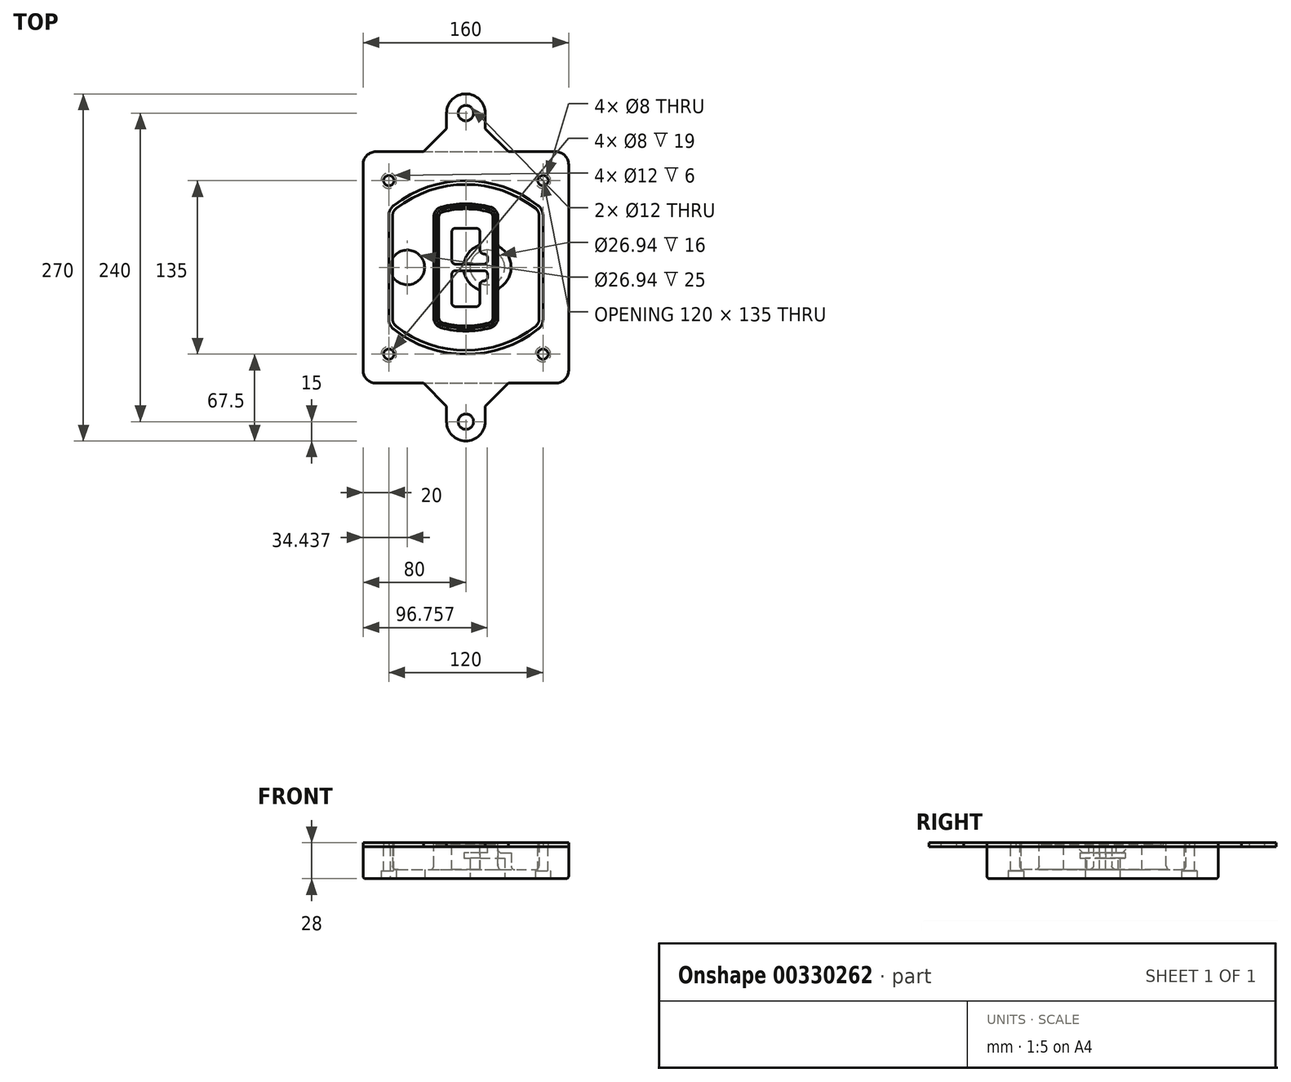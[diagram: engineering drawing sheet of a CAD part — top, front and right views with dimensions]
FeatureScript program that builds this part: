
annotation { "Feature Type Name" : "Feature", "Feature Type Description" : "" }
export const myFeature = defineFeature(function(context is Context, id is Id, definition is map)
    precondition{}
    {
        {
            var Q0;
            Q0=qCreatedBy(makeId("Top.planeOp"),FACE);
            var sketch = newSketch(context, id + "F0", { "sketchPlane" : qUnion([Q0])});
            skPoint(sketch, "E0.rect.middle", {"position": v(0, 0) * mm});
            skLineSegment(sketch, "E1.bottom", {"start": v(-70, -90) * mm, "end": v(70, -90) * mm});
            skLineSegment(sketch, "E1.top", {"start": v(-70, 90) * mm, "end": v(70, 90) * mm});
            skLineSegment(sketch, "E1.left", {"start": v(-80, -80) * mm, "end": v(-80, 80) * mm});
            skLineSegment(sketch, "E1.right", {"start": v(80, -80) * mm, "end": v(80, 80) * mm});
            skLineSegment(sketch, "E2", {"start": v(-80, 90) * mm, "end": v(80, -90) * mm, "construction": true});
            skLineSegment(sketch, "E3", {"start": v(80, 90) * mm, "end": v(-80, -90) * mm, "construction": true});
            skCircle(sketch, "E4", {"center": v(-60, 67.5) * mm, "radius": 4 * mm});
            skCircle(sketch, "E5", {"center": v(60, 67.5) * mm, "radius": 4 * mm});
            skCircle(sketch, "E6", {"center": v(60, -67.5) * mm, "radius": 4 * mm});
            skCircle(sketch, "E7", {"center": v(-60, -67.5) * mm, "radius": 4 * mm});
            skLineSegment(sketch, "E8", {"start": v(-60, 67.5) * mm, "end": v(60, 67.5) * mm, "construction": true});
            skLineSegment(sketch, "E9", {"start": v(60, 67.5) * mm, "end": v(60, -67.5) * mm, "construction": true});
            skLineSegment(sketch, "E10", {"start": v(60, -67.5) * mm, "end": v(-60, -67.5) * mm, "construction": true});
            skLineSegment(sketch, "E11", {"start": v(-60, -67.5) * mm, "end": v(-60, 67.5) * mm, "construction": true});
            skLineSegment(sketch, "E12", {"start": v(-60, 40.3) * mm, "end": v(-60, -40.3) * mm});
            skLineSegment(sketch, "E13", {"start": v(60, 40.3) * mm, "end": v(60, -40.3) * mm});
            skArc(sketch, "E14", {"start": v(56.15, 48.18) * mm, "mid": v(0, 67.5) * mm, "end": v(-56.15, 48.18) * mm});
            skArc(sketch, "E15", {"start": v(-56.15, -48.18) * mm, "mid": v(0, -67.5) * mm, "end": v(56.15, -48.18) * mm});
            skLineSegment(sketch, "E16", {"start": v(-60, 0) * mm, "end": v(60, 0) * mm, "construction": true});
            skPoint(sketch, "E17.visualSharp", {"position": v(-60, -45) * mm});
            skArc(sketch, "E17.filletArc", {"start": v(-60, -40.3) * mm, "mid": v(-58.99, -44.68) * mm, "end": v(-56.15, -48.18) * mm});
            skPoint(sketch, "E18.visualSharp", {"position": v(-60, 45) * mm});
            skArc(sketch, "E18.filletArc", {"start": v(-56.15, 48.18) * mm, "mid": v(-58.99, 44.68) * mm, "end": v(-60, 40.3) * mm});
            skPoint(sketch, "E19.visualSharp", {"position": v(60, 45) * mm});
            skArc(sketch, "E19.filletArc", {"start": v(60, 40.3) * mm, "mid": v(58.99, 44.68) * mm, "end": v(56.15, 48.18) * mm});
            skPoint(sketch, "E20.visualSharp", {"position": v(60, -45) * mm});
            skArc(sketch, "E20.filletArc", {"start": v(56.15, -48.18) * mm, "mid": v(58.99, -44.68) * mm, "end": v(60, -40.3) * mm});
            skPoint(sketch, "E21.visualSharp", {"position": v(-80, 90) * mm});
            skArc(sketch, "E21.filletArc", {"start": v(-70, 90) * mm, "mid": v(-77.07, 87.07) * mm, "end": v(-80, 80) * mm});
            skPoint(sketch, "E22.visualSharp", {"position": v(80, 90) * mm});
            skArc(sketch, "E22.filletArc", {"start": v(80, 80) * mm, "mid": v(77.07, 87.07) * mm, "end": v(70, 90) * mm});
            skPoint(sketch, "E23.visualSharp", {"position": v(80, -90) * mm});
            skArc(sketch, "E23.filletArc", {"start": v(70, -90) * mm, "mid": v(77.07, -87.07) * mm, "end": v(80, -80) * mm});
            skPoint(sketch, "E24.visualSharp", {"position": v(-80, -90) * mm});
            skArc(sketch, "E24.filletArc", {"start": v(-80, -80) * mm, "mid": v(-77.07, -87.07) * mm, "end": v(-70, -90) * mm});
            skArc(sketch, "E25.0", {"start": v(57, 40.3) * mm, "mid": v(56.3, 43.36) * mm, "end": v(54.3, 45.81) * mm});
            skLineSegment(sketch, "E25.1", {"start": v(57, 40.3) * mm, "end": v(57, -40.3) * mm});
            skArc(sketch, "E25.2", {"start": v(54.3, -45.81) * mm, "mid": v(56.3, -43.36) * mm, "end": v(57, -40.3) * mm});
            skArc(sketch, "E25.3", {"start": v(-54.3, -45.81) * mm, "mid": v(0, -64.5) * mm, "end": v(54.3, -45.81) * mm});
            skArc(sketch, "E25.4", {"start": v(-57, -40.3) * mm, "mid": v(-56.3, -43.36) * mm, "end": v(-54.3, -45.81) * mm});
            skArc(sketch, "E25.5", {"start": v(54.3, 45.81) * mm, "mid": v(0, 64.5) * mm, "end": v(-54.3, 45.81) * mm});
            skLineSegment(sketch, "E25.6", {"start": v(-57, 40.3) * mm, "end": v(-57, -40.3) * mm});
            skArc(sketch, "E25.7", {"start": v(-54.3, 45.81) * mm, "mid": v(-56.3, 43.36) * mm, "end": v(-57, 40.3) * mm});
            skArc(sketch, "E26.0", {"start": v(-58.62, 51.33) * mm, "mid": v(-62.58, 46.43) * mm, "end": v(-64, 40.3) * mm});
            skArc(sketch, "E26.1", {"start": v(58.62, 51.33) * mm, "mid": v(0, 71.5) * mm, "end": v(-58.62, 51.33) * mm});
            skArc(sketch, "E26.2", {"start": v(64, 40.3) * mm, "mid": v(62.58, 46.43) * mm, "end": v(58.62, 51.33) * mm});
            skLineSegment(sketch, "E26.3", {"start": v(64, 40.3) * mm, "end": v(64, -40.3) * mm});
            skArc(sketch, "E26.4", {"start": v(58.62, -51.33) * mm, "mid": v(62.58, -46.43) * mm, "end": v(64, -40.3) * mm});
            skLineSegment(sketch, "E26.5", {"start": v(-64, 40.3) * mm, "end": v(-64, -40.3) * mm});
            skArc(sketch, "E26.6", {"start": v(-58.62, -51.33) * mm, "mid": v(0, -71.5) * mm, "end": v(58.62, -51.33) * mm});
            skArc(sketch, "E26.7", {"start": v(-64, -40.3) * mm, "mid": v(-62.58, -46.43) * mm, "end": v(-58.62, -51.33) * mm});
            skSolve(sketch);
        }
        {
            var Q0;
            Q0=makeQuery(id+"F0.imprint","IMPRINT",FACE,{"disambiguationData":[TD([[makeQuery(id+"F0.imprint","IMPRINT",EDGE,{"derivedFrom":sQuery(id+"F0.wireOp",EDGE,"E1.bottom")}),1.0]])]});
            var Q1;
            Q1=makeQuery(id+"F0.imprint","IMPRINT",FACE,{"disambiguationData":[TD([[makeQuery(id+"F0.imprint","IMPRINT",EDGE,{"derivedFrom":sQuery(id+"F0.wireOp",EDGE,"E12")}),1.0]])]});
            var Q2;
            Q2=makeQuery(id+"F0.imprint","IMPRINT",FACE,{"disambiguationData":[TD([[makeQuery(id+"F0.imprint","IMPRINT",EDGE,{"derivedFrom":sQuery(id+"F0.wireOp",EDGE,"E25.0")}),1.0]])]});
            var Q3;
            Q3=makeQuery(id+"F0.imprint","IMPRINT",FACE,{"disambiguationData":[TD([[makeQuery(id+"F0.imprint","IMPRINT",EDGE,{"derivedFrom":sQuery(id+"F0.wireOp",EDGE,"E12")}),-1.0]])]});
            extrude(context, id + "F1", {"entities" : qUnion([Q0, Q1, Q2, Q3]), "oppositeDirection" : true, "depth" : 25 * mm});
        }
        {
            var Q0;
            Q0=makeQuery(id+"F0.imprint","IMPRINT",FACE,{"disambiguationData":[TD([[makeQuery(id+"F0.imprint","IMPRINT",EDGE,{"derivedFrom":sQuery(id+"F0.wireOp",EDGE,"E12")}),1.0]])]});
            extrude(context, id + "F2", {"entities" : qUnion([Q0]), "operationType" : NewBodyOperationType.ADD, "depth" : 3 * mm});
        }
        {
            var Q0;
            Q0=makeQuery(id+"F0.imprint","IMPRINT",FACE,{"disambiguationData":[TD([[makeQuery(id+"F0.imprint","IMPRINT",EDGE,{"derivedFrom":sQuery(id+"F0.wireOp",EDGE,"E25.0")}),1.0]])]});
            extrude(context, id + "F3", {"entities" : qUnion([Q0]), "operationType" : NewBodyOperationType.REMOVE, "oppositeDirection" : true, "depth" : 18 * mm});
        }
        {
            var Q0;
            Q0=makeQuery(id+"F2.opExtrude","CAP_FACE",FACE,{"disambiguationData":[OSD([sQuery(id+"F0.wireOp",EDGE,"E12"),sQuery(id+"F0.wireOp",EDGE,"E13"),sQuery(id+"F0.wireOp",EDGE,"E14"),sQuery(id+"F0.wireOp",EDGE,"E15"),sQuery(id+"F0.wireOp",EDGE,"E17.filletArc"),sQuery(id+"F0.wireOp",EDGE,"E18.filletArc"),sQuery(id+"F0.wireOp",EDGE,"E19.filletArc"),sQuery(id+"F0.wireOp",EDGE,"E20.filletArc"),sQuery(id+"F0.wireOp",EDGE,"E25.0"),sQuery(id+"F0.wireOp",EDGE,"E25.1"),sQuery(id+"F0.wireOp",EDGE,"E25.2"),sQuery(id+"F0.wireOp",EDGE,"E25.3"),sQuery(id+"F0.wireOp",EDGE,"E25.4"),sQuery(id+"F0.wireOp",EDGE,"E25.5"),sQuery(id+"F0.wireOp",EDGE,"E25.6"),sQuery(id+"F0.wireOp",EDGE,"E25.7")])],"isStart":false});
            var sketch = newSketch(context, id + "F4", { "sketchPlane" : qUnion([Q0])});
            skArc(sketch, "E27.0", {"start": v(-19.08, -46.97) * mm, "mid": v(0, -49.5) * mm, "end": v(19.08, -46.97) * mm});
            skArc(sketch, "E28.0", {"start": v(19.08, 46.97) * mm, "mid": v(0, 49.5) * mm, "end": v(-19.08, 46.97) * mm});
            skLineSegment(sketch, "E29", {"start": v(-25, 39.25) * mm, "end": v(-25, -39.25) * mm});
            skLineSegment(sketch, "E30", {"start": v(25, 39.25) * mm, "end": v(25, -39.25) * mm});
            skLineSegment(sketch, "E31", {"start": v(-25, 45.1) * mm, "end": v(25, 45.1) * mm, "construction": true});
            skLineSegment(sketch, "E32", {"start": v(-25, -45.1) * mm, "end": v(25, -45.1) * mm, "construction": true});
            skPoint(sketch, "E33.visualSharp", {"position": v(-25, 45.1) * mm});
            skArc(sketch, "E33.filletArc", {"start": v(-19.08, 46.97) * mm, "mid": v(-23.35, 44.11) * mm, "end": v(-25, 39.25) * mm});
            skPoint(sketch, "E34.visualSharp", {"position": v(25, 45.1) * mm});
            skArc(sketch, "E34.filletArc", {"start": v(25, 39.25) * mm, "mid": v(23.35, 44.11) * mm, "end": v(19.08, 46.97) * mm});
            skPoint(sketch, "E35.visualSharp", {"position": v(25, -45.1) * mm});
            skArc(sketch, "E35.filletArc", {"start": v(19.08, -46.97) * mm, "mid": v(23.35, -44.11) * mm, "end": v(25, -39.25) * mm});
            skPoint(sketch, "E36.visualSharp", {"position": v(-25, -45.1) * mm});
            skArc(sketch, "E36.filletArc", {"start": v(-25, -39.25) * mm, "mid": v(-23.35, -44.11) * mm, "end": v(-19.08, -46.97) * mm});
            skArc(sketch, "E37.0", {"start": v(54.3, 45.81) * mm, "mid": v(0, 64.5) * mm, "end": v(-54.3, 45.81) * mm});
            skArc(sketch, "E37.1", {"start": v(-54.3, 45.81) * mm, "mid": v(-56.3, 43.36) * mm, "end": v(-57, 40.3) * mm});
            skLineSegment(sketch, "E37.2", {"start": v(-57, 40.3) * mm, "end": v(-57, -40.3) * mm});
            skArc(sketch, "E37.3", {"start": v(-57, -40.3) * mm, "mid": v(-56.3, -43.36) * mm, "end": v(-54.3, -45.81) * mm});
            skArc(sketch, "E37.4", {"start": v(-54.3, -45.81) * mm, "mid": v(0, -64.5) * mm, "end": v(54.3, -45.81) * mm});
            skArc(sketch, "E37.5", {"start": v(54.3, -45.81) * mm, "mid": v(56.3, -43.36) * mm, "end": v(57, -40.3) * mm});
            skLineSegment(sketch, "E37.6", {"start": v(57, 40.3) * mm, "end": v(57, -40.3) * mm});
            skArc(sketch, "E37.7", {"start": v(57, 40.3) * mm, "mid": v(56.3, 43.36) * mm, "end": v(54.3, 45.81) * mm});
            skLineSegment(sketch, "E38.0", {"start": v(23, 39.25) * mm, "end": v(23, -39.25) * mm});
            skArc(sketch, "E38.1", {"start": v(18.56, -45.04) * mm, "mid": v(21.76, -42.9) * mm, "end": v(23, -39.25) * mm});
            skArc(sketch, "E38.2", {"start": v(-18.56, -45.04) * mm, "mid": v(0, -47.5) * mm, "end": v(18.56, -45.04) * mm});
            skArc(sketch, "E38.3", {"start": v(-23, -39.25) * mm, "mid": v(-21.76, -42.9) * mm, "end": v(-18.56, -45.04) * mm});
            skLineSegment(sketch, "E38.4", {"start": v(-23, 39.25) * mm, "end": v(-23, -39.25) * mm});
            skArc(sketch, "E38.5", {"start": v(23, 39.25) * mm, "mid": v(21.76, 42.9) * mm, "end": v(18.56, 45.04) * mm});
            skArc(sketch, "E38.6", {"start": v(-18.56, 45.04) * mm, "mid": v(-21.76, 42.9) * mm, "end": v(-23, 39.25) * mm});
            skArc(sketch, "E38.7", {"start": v(18.56, 45.04) * mm, "mid": v(0, 47.5) * mm, "end": v(-18.56, 45.04) * mm});
            skArc(sketch, "E39.0", {"start": v(21, 39.25) * mm, "mid": v(20.18, 41.68) * mm, "end": v(18.04, 43.1) * mm});
            skLineSegment(sketch, "E39.1", {"start": v(21, 39.25) * mm, "end": v(21, -39.25) * mm});
            skArc(sketch, "E39.2", {"start": v(18.04, -43.1) * mm, "mid": v(20.18, -41.68) * mm, "end": v(21, -39.25) * mm});
            skArc(sketch, "E39.3", {"start": v(-18.04, -43.1) * mm, "mid": v(0, -45.5) * mm, "end": v(18.04, -43.1) * mm});
            skArc(sketch, "E39.4", {"start": v(-21, -39.25) * mm, "mid": v(-20.18, -41.68) * mm, "end": v(-18.04, -43.1) * mm});
            skArc(sketch, "E39.5", {"start": v(18.04, 43.1) * mm, "mid": v(0, 45.5) * mm, "end": v(-18.04, 43.1) * mm});
            skLineSegment(sketch, "E39.6", {"start": v(-21, 39.25) * mm, "end": v(-21, -39.25) * mm});
            skArc(sketch, "E39.7", {"start": v(-18.04, 43.1) * mm, "mid": v(-20.18, 41.68) * mm, "end": v(-21, 39.25) * mm});
            skLineSegment(sketch, "E40", {"start": v(-25, 0) * mm, "end": v(25, 0) * mm, "construction": true});
            skLineSegment(sketch, "E41", {"start": v(-11, 5.5) * mm, "end": v(-11, 27.5) * mm});
            skLineSegment(sketch, "E42", {"start": v(-8, 30.5) * mm, "end": v(8, 30.5) * mm});
            skLineSegment(sketch, "E43", {"start": v(11, 27.5) * mm, "end": v(11, 13.5) * mm});
            skLineSegment(sketch, "E44", {"start": v(14, 10.5) * mm, "end": v(14, 10.5) * mm});
            skLineSegment(sketch, "E45", {"start": v(17, 7.5) * mm, "end": v(17, 5.5) * mm});
            skLineSegment(sketch, "E46", {"start": v(14, 2.5) * mm, "end": v(-8, 2.5) * mm});
            skPoint(sketch, "E47.visualSharp", {"position": v(-11, 30.5) * mm});
            skArc(sketch, "E47.filletArc", {"start": v(-8, 30.5) * mm, "mid": v(-10.12, 29.62) * mm, "end": v(-11, 27.5) * mm});
            skPoint(sketch, "E48.visualSharp", {"position": v(11, 30.5) * mm});
            skArc(sketch, "E48.filletArc", {"start": v(11, 27.5) * mm, "mid": v(10.12, 29.62) * mm, "end": v(8, 30.5) * mm});
            skPoint(sketch, "E49.visualSharp", {"position": v(11, 10.5) * mm});
            skArc(sketch, "E49.filletArc", {"start": v(11, 13.5) * mm, "mid": v(11.88, 11.38) * mm, "end": v(14, 10.5) * mm});
            skPoint(sketch, "E50.visualSharp", {"position": v(17, 10.5) * mm});
            skArc(sketch, "E50.filletArc", {"start": v(17, 7.5) * mm, "mid": v(16.12, 9.62) * mm, "end": v(14, 10.5) * mm});
            skPoint(sketch, "E51.visualSharp", {"position": v(17, 2.5) * mm});
            skArc(sketch, "E51.filletArc", {"start": v(14, 2.5) * mm, "mid": v(16.12, 3.38) * mm, "end": v(17, 5.5) * mm});
            skPoint(sketch, "E52.visualSharp", {"position": v(-11, 2.5) * mm});
            skArc(sketch, "E52.filletArc", {"start": v(-11, 5.5) * mm, "mid": v(-10.12, 3.38) * mm, "end": v(-8, 2.5) * mm});
            skLineSegment(sketch, "E53.0.MirrorCS", {"start": v(14, -2.5) * mm, "end": v(-8, -2.5) * mm});
            skArc(sketch, "E54.0.MirrorCS", {"start": v(-11, -5.5) * mm, "mid": v(-10.12, -3.38) * mm, "end": v(-8, -2.5) * mm});
            skLineSegment(sketch, "E55.0.MirrorCS", {"start": v(-11, -5.5) * mm, "end": v(-11, -27.5) * mm});
            skArc(sketch, "E56.0.MirrorCS", {"start": v(-8, -30.5) * mm, "mid": v(-10.12, -29.62) * mm, "end": v(-11, -27.5) * mm});
            skLineSegment(sketch, "E57.0.MirrorCS", {"start": v(-8, -30.5) * mm, "end": v(8, -30.5) * mm});
            skArc(sketch, "E58.0.MirrorCS", {"start": v(11, -27.5) * mm, "mid": v(10.12, -29.62) * mm, "end": v(8, -30.5) * mm});
            skLineSegment(sketch, "E59.0.MirrorCS", {"start": v(11, -27.5) * mm, "end": v(11, -13.5) * mm});
            skArc(sketch, "E60.0.MirrorCS", {"start": v(11, -13.5) * mm, "mid": v(11.88, -11.38) * mm, "end": v(14, -10.5) * mm});
            skArc(sketch, "E61.0.MirrorCS", {"start": v(17, -7.5) * mm, "mid": v(16.12, -9.62) * mm, "end": v(14, -10.5) * mm});
            skLineSegment(sketch, "E62.0.MirrorCS", {"start": v(17, -7.5) * mm, "end": v(17, -5.5) * mm});
            skArc(sketch, "E63.0.MirrorCS", {"start": v(14, -2.5) * mm, "mid": v(16.12, -3.38) * mm, "end": v(17, -5.5) * mm});
            skSolve(sketch);
        }
        {
            var Q0;
            Q0=makeQuery(id+"F4.imprint","IMPRINT",FACE,{"disambiguationData":[TD([[makeQuery(id+"F4.imprint","IMPRINT",EDGE,{"derivedFrom":sQuery(id+"F4.wireOp",EDGE,"E27.0")}),1.0]])]});
            var Q1;
            Q1=makeQuery(id+"F4.imprint","IMPRINT",FACE,{"disambiguationData":[TD([[makeQuery(id+"F4.imprint","IMPRINT",EDGE,{"derivedFrom":sQuery(id+"F4.wireOp",EDGE,"E38.0")}),-1.0]])]});
            var Q2;
            Q2=makeQuery(id+"F4.imprint","IMPRINT",FACE,{"disambiguationData":[TD([[makeQuery(id+"F4.imprint","IMPRINT",EDGE,{"derivedFrom":sQuery(id+"F4.wireOp",EDGE,"E39.0")}),1.0]])]});
            extrude(context, id + "F5", {"entities" : qUnion([Q0, Q1, Q2]), "operationType" : NewBodyOperationType.ADD, "endBound" : BoundingType.UP_TO_NEXT, "oppositeDirection" : true, "depth" : 25 * mm});
        }
        {
            var Q0;
            Q0=makeQuery(id+"F4.imprint","IMPRINT",FACE,{"disambiguationData":[TD([[makeQuery(id+"F4.imprint","IMPRINT",EDGE,{"derivedFrom":sQuery(id+"F4.wireOp",EDGE,"E38.0")}),-1.0]])]});
            extrude(context, id + "F6", {"entities" : qUnion([Q0]), "operationType" : NewBodyOperationType.REMOVE, "oppositeDirection" : true, "depth" : 2 * mm});
        }
        {
            var Q0;
            Q0=makeQuery(id+"F1.opExtrude","CAP_FACE",FACE,{"disambiguationData":[OSD([sQuery(id+"F0.wireOp",EDGE,"E1.bottom"),sQuery(id+"F0.wireOp",EDGE,"E1.top"),sQuery(id+"F0.wireOp",EDGE,"E1.left"),sQuery(id+"F0.wireOp",EDGE,"E1.right"),sQuery(id+"F0.wireOp",EDGE,"E4"),sQuery(id+"F0.wireOp",EDGE,"E5"),sQuery(id+"F0.wireOp",EDGE,"E6"),sQuery(id+"F0.wireOp",EDGE,"E7"),sQuery(id+"F0.wireOp",EDGE,"E21.filletArc"),sQuery(id+"F0.wireOp",EDGE,"E22.filletArc"),sQuery(id+"F0.wireOp",EDGE,"E23.filletArc"),sQuery(id+"F0.wireOp",EDGE,"E24.filletArc")])],"isStart":false});
            var sketch = newSketch(context, id + "F7", { "sketchPlane" : qUnion([Q0])});
            skCircle(sketch, "E64", {"center": v(16.76, 0) * mm, "radius": 13.47 * mm});
            skCircle(sketch, "E65", {"center": v(-45.56, 0) * mm, "radius": 13.47 * mm});
            skLineSegment(sketch, "E66", {"start": v(80, 0) * mm, "end": v(-80, 0) * mm});
            skCircle(sketch, "E67", {"center": v(16.76, 0) * mm, "radius": 18.47 * mm});
            skCircle(sketch, "E68", {"center": v(60, -67.5) * mm, "radius": 6 * mm});
            skCircle(sketch, "E69", {"center": v(-60, -67.5) * mm, "radius": 6 * mm});
            skCircle(sketch, "E70", {"center": v(-60, 67.5) * mm, "radius": 6 * mm});
            skCircle(sketch, "E71", {"center": v(60, 67.5) * mm, "radius": 6 * mm});
            skSolve(sketch);
        }
        {
            var Q0;
            {var subQ1=sQuery(id+"F7.wireOp",EDGE,"E66");var subQ4=sQuery(id+"F7.wireOp",EDGE,"E64");var subQ6=makeQuery(id+"F7.imprint","INTERSECT",VERTEX,{"disambiguationData":[OD(0.0)],"derivedFrom":[subQ4,subQ1]});Q0=makeQuery(id+"F7.imprint","IMPRINT",FACE,{"disambiguationData":[TD([[makeQuery(id+"F7.imprint","IMPRINT",EDGE,{"disambiguationData":[TD([[subQ6,-1.0]])],"derivedFrom":subQ4}),-1.0]])]});}
            var Q1;
            {var subQ0=sQuery(id+"F7.wireOp",EDGE,"E66");var subQ1=sQuery(id+"F7.wireOp",EDGE,"E64");var subQ3=makeQuery(id+"F7.imprint","INTERSECT",VERTEX,{"disambiguationData":[OD(0.0)],"derivedFrom":[subQ1,subQ0]});Q1=makeQuery(id+"F7.imprint","IMPRINT",FACE,{"disambiguationData":[TD([[makeQuery(id+"F7.imprint","IMPRINT",EDGE,{"disambiguationData":[TD([[subQ3,-1.0]])],"derivedFrom":subQ1}),1.0]])]});}
            var Q2;
            {var subQ0=sQuery(id+"F7.wireOp",EDGE,"E66");var subQ1=sQuery(id+"F7.wireOp",EDGE,"E64");var subQ3=makeQuery(id+"F7.imprint","INTERSECT",VERTEX,{"disambiguationData":[OD(0.0)],"derivedFrom":[subQ1,subQ0]});Q2=makeQuery(id+"F7.imprint","IMPRINT",FACE,{"disambiguationData":[TD([[makeQuery(id+"F7.imprint","IMPRINT",EDGE,{"disambiguationData":[TD([[subQ3,1.0]])],"derivedFrom":subQ1}),1.0]])]});}
            var Q3;
            {var subQ1=sQuery(id+"F7.wireOp",EDGE,"E66");var subQ4=sQuery(id+"F7.wireOp",EDGE,"E64");var subQ6=makeQuery(id+"F7.imprint","INTERSECT",VERTEX,{"disambiguationData":[OD(0.0)],"derivedFrom":[subQ4,subQ1]});Q3=makeQuery(id+"F7.imprint","IMPRINT",FACE,{"disambiguationData":[TD([[makeQuery(id+"F7.imprint","IMPRINT",EDGE,{"disambiguationData":[TD([[subQ6,1.0]])],"derivedFrom":subQ4}),-1.0]])]});}
            extrude(context, id + "F8", {"entities" : qUnion([Q0, Q1, Q2, Q3]), "operationType" : NewBodyOperationType.ADD, "oppositeDirection" : true, "depth" : 20 * mm});
        }
        {
            var Q0;
            {var subQ0=sQuery(id+"F7.wireOp",EDGE,"E66");var subQ1=sQuery(id+"F7.wireOp",EDGE,"E64");var subQ3=makeQuery(id+"F7.imprint","INTERSECT",VERTEX,{"disambiguationData":[OD(0.0)],"derivedFrom":[subQ1,subQ0]});Q0=makeQuery(id+"F7.imprint","IMPRINT",FACE,{"disambiguationData":[TD([[makeQuery(id+"F7.imprint","IMPRINT",EDGE,{"disambiguationData":[TD([[subQ3,-1.0]])],"derivedFrom":subQ1}),1.0]])]});}
            var Q1;
            {var subQ0=sQuery(id+"F7.wireOp",EDGE,"E66");var subQ1=sQuery(id+"F7.wireOp",EDGE,"E64");var subQ3=makeQuery(id+"F7.imprint","INTERSECT",VERTEX,{"disambiguationData":[OD(0.0)],"derivedFrom":[subQ1,subQ0]});Q1=makeQuery(id+"F7.imprint","IMPRINT",FACE,{"disambiguationData":[TD([[makeQuery(id+"F7.imprint","IMPRINT",EDGE,{"disambiguationData":[TD([[subQ3,1.0]])],"derivedFrom":subQ1}),1.0]])]});}
            extrude(context, id + "F9", {"entities" : qUnion([Q0, Q1]), "operationType" : NewBodyOperationType.REMOVE, "oppositeDirection" : true, "depth" : 16 * mm});
        }
        {
            var Q0;
            {var subQ0=sQuery(id+"F7.wireOp",EDGE,"E66");var subQ1=sQuery(id+"F7.wireOp",EDGE,"E65");var subQ3=makeQuery(id+"F7.imprint","INTERSECT",VERTEX,{"disambiguationData":[OD(0.0)],"derivedFrom":[subQ1,subQ0]});Q0=makeQuery(id+"F7.imprint","IMPRINT",FACE,{"disambiguationData":[TD([[makeQuery(id+"F7.imprint","IMPRINT",EDGE,{"disambiguationData":[TD([[subQ3,-1.0]])],"derivedFrom":subQ1}),1.0]])]});}
            var Q1;
            {var subQ0=sQuery(id+"F7.wireOp",EDGE,"E66");var subQ1=sQuery(id+"F7.wireOp",EDGE,"E65");var subQ3=makeQuery(id+"F7.imprint","INTERSECT",VERTEX,{"disambiguationData":[OD(0.0)],"derivedFrom":[subQ1,subQ0]});Q1=makeQuery(id+"F7.imprint","IMPRINT",FACE,{"disambiguationData":[TD([[makeQuery(id+"F7.imprint","IMPRINT",EDGE,{"disambiguationData":[TD([[subQ3,1.0]])],"derivedFrom":subQ1}),1.0]])]});}
            extrude(context, id + "F10", {"entities" : qUnion([Q0, Q1]), "operationType" : NewBodyOperationType.REMOVE, "oppositeDirection" : true, "depth" : 25 * mm});
        }
        {
            var Q0;
            Q0=makeQuery(id+"F7.imprint","IMPRINT",FACE,{"disambiguationData":[TD([[makeQuery(id+"F7.imprint","IMPRINT",EDGE,{"derivedFrom":sQuery(id+"F7.wireOp",EDGE,"E68")}),1.0]])]});
            var Q1;
            Q1=makeQuery(id+"F7.imprint","IMPRINT",FACE,{"disambiguationData":[TD([[makeQuery(id+"F7.imprint","IMPRINT",EDGE,{"derivedFrom":makeQuery(id+"F1.opExtrude","CAP_EDGE",EDGE,{"disambiguationData":[OSD([sQuery(id+"F0.wireOp",EDGE,"E5")])],"isStart":false})}),-1.0]])]});
            var Q2;
            Q2=makeQuery(id+"F7.imprint","IMPRINT",FACE,{"disambiguationData":[TD([[makeQuery(id+"F7.imprint","IMPRINT",EDGE,{"derivedFrom":sQuery(id+"F7.wireOp",EDGE,"E69")}),1.0]])]});
            var Q3;
            Q3=makeQuery(id+"F7.imprint","IMPRINT",FACE,{"disambiguationData":[TD([[makeQuery(id+"F7.imprint","IMPRINT",EDGE,{"derivedFrom":makeQuery(id+"F1.opExtrude","CAP_EDGE",EDGE,{"disambiguationData":[OSD([sQuery(id+"F0.wireOp",EDGE,"E4")])],"isStart":false})}),-1.0]])]});
            var Q4;
            Q4=makeQuery(id+"F7.imprint","IMPRINT",FACE,{"disambiguationData":[TD([[makeQuery(id+"F7.imprint","IMPRINT",EDGE,{"derivedFrom":sQuery(id+"F7.wireOp",EDGE,"E70")}),1.0]])]});
            var Q5;
            Q5=makeQuery(id+"F7.imprint","IMPRINT",FACE,{"disambiguationData":[TD([[makeQuery(id+"F7.imprint","IMPRINT",EDGE,{"derivedFrom":makeQuery(id+"F1.opExtrude","CAP_EDGE",EDGE,{"disambiguationData":[OSD([sQuery(id+"F0.wireOp",EDGE,"E7")])],"isStart":false})}),-1.0]])]});
            var Q6;
            Q6=makeQuery(id+"F7.imprint","IMPRINT",FACE,{"disambiguationData":[TD([[makeQuery(id+"F7.imprint","IMPRINT",EDGE,{"derivedFrom":sQuery(id+"F7.wireOp",EDGE,"E71")}),1.0]])]});
            var Q7;
            Q7=makeQuery(id+"F7.imprint","IMPRINT",FACE,{"disambiguationData":[TD([[makeQuery(id+"F7.imprint","IMPRINT",EDGE,{"derivedFrom":makeQuery(id+"F1.opExtrude","CAP_EDGE",EDGE,{"disambiguationData":[OSD([sQuery(id+"F0.wireOp",EDGE,"E6")])],"isStart":false})}),-1.0]])]});
            extrude(context, id + "F11", {"entities" : qUnion([Q0, Q1, Q2, Q3, Q4, Q5, Q6, Q7]), "operationType" : NewBodyOperationType.REMOVE, "oppositeDirection" : true, "depth" : 6 * mm});
        }
        {
            var Q0;
            Q0=makeQuery(id+"F9.boolean.opBoolean","COPY",FACE,{"derivedFrom":makeQuery(id+"F9.opExtrude","CAP_FACE",FACE,{"disambiguationData":[OSD([sQuery(id+"F7.wireOp",EDGE,"E64")])],"isStart":false})});
            var sketch = newSketch(context, id + "F12", { "sketchPlane" : qUnion([Q0])});
            skArc(sketch, "E72.0", {"start": v(11, 17.55) * mm, "mid": v(2.57, 11.82) * mm, "end": v(-1.54, 2.5) * mm});
            skArc(sketch, "E72.1", {"start": v(-1.54, -2.5) * mm, "mid": v(2.57, -11.82) * mm, "end": v(11, -17.55) * mm});
            skLineSegment(sketch, "E73", {"start": v(-1.54, -2.5) * mm, "end": v(14, -2.5) * mm});
            skLineSegment(sketch, "E74.0", {"start": v(14, 2.5) * mm, "end": v(-1.54, 2.5) * mm});
            skArc(sketch, "E74.1", {"start": v(14, 2.5) * mm, "mid": v(16.12, 3.38) * mm, "end": v(17, 5.5) * mm});
            skLineSegment(sketch, "E74.2", {"start": v(17, 7.5) * mm, "end": v(17, 5.5) * mm});
            skArc(sketch, "E74.3", {"start": v(17, 7.5) * mm, "mid": v(16.12, 9.62) * mm, "end": v(14, 10.5) * mm});
            skArc(sketch, "E74.4", {"start": v(11, 13.5) * mm, "mid": v(11.88, 11.38) * mm, "end": v(14, 10.5) * mm});
            skLineSegment(sketch, "E74.5", {"start": v(11, 17.55) * mm, "end": v(11, 13.5) * mm});
            skLineSegment(sketch, "E74.7", {"start": v(14, -2.5) * mm, "end": v(-1.54, -2.5) * mm});
            skArc(sketch, "E74.8", {"start": v(14, -2.5) * mm, "mid": v(16.12, -3.38) * mm, "end": v(17, -5.5) * mm});
            skLineSegment(sketch, "E74.9", {"start": v(17, -7.5) * mm, "end": v(17, -5.5) * mm});
            skArc(sketch, "E74.10", {"start": v(17, -7.5) * mm, "mid": v(16.12, -9.62) * mm, "end": v(14, -10.5) * mm});
            skArc(sketch, "E74.11", {"start": v(11, -13.5) * mm, "mid": v(11.88, -11.38) * mm, "end": v(14, -10.5) * mm});
            skLineSegment(sketch, "E74.12", {"start": v(11, -17.55) * mm, "end": v(11, -13.5) * mm});
            skPoint(sketch, "E75.orphan", {"position": v(11, -27.5) * mm});
            skPoint(sketch, "E76.orphan", {"position": v(-8, -2.5) * mm});
            skPoint(sketch, "E77.orphan", {"position": v(-8, 2.5) * mm});
            skPoint(sketch, "E78.orphan", {"position": v(11, 27.5) * mm});
            skSolve(sketch);
        }
        {
            var Q0;
            {var subQ7=sQuery(id+"F12.wireOp",EDGE,"E72.0");var subQ14=sQuery(id+"F12.wireOp",EDGE,"E72.1");var subQ16=sQuery(id+"F12.wireOp",EDGE,"E74.1");var subQ18=sQuery(id+"F12.wireOp",EDGE,"E74.8");Q0=qUnion([makeQuery(id+"F12.imprint","IMPRINT",FACE,{"disambiguationData":[TD([[makeQuery(id+"F12.imprint","IMPRINT",EDGE,{"derivedFrom":subQ7}),1.0]])]}),makeQuery(id+"F12.imprint","IMPRINT",FACE,{"disambiguationData":[TD([[makeQuery(id+"F12.imprint","IMPRINT",EDGE,{"derivedFrom":subQ14}),1.0]])]}),makeQuery(id+"F12.imprint","IMPRINT",FACE,{"disambiguationData":[TD([[makeQuery(id+"F12.imprint","IMPRINT",EDGE,{"derivedFrom":subQ16}),1.0]])]}),makeQuery(id+"F12.imprint","IMPRINT",FACE,{"disambiguationData":[TD([[makeQuery(id+"F12.imprint","IMPRINT",EDGE,{"derivedFrom":subQ18}),-1.0]])]})]);}
            var Q1;
            Q1=makeQuery(id+"F5.boolean.opBoolean","SPLIT",FACE,{"disambiguationData":[TD([makeQuery(id+"F5.opExtrude","SWEPT_FACE",FACE,{"disambiguationData":[OSD([sQuery(id+"F4.wireOp",EDGE,"E41")])]})])],"derivedFrom":makeQuery(id+"F3.boolean.opBoolean","COPY",FACE,{"derivedFrom":makeQuery(id+"F3.opExtrude","CAP_FACE",FACE,{"disambiguationData":[OSD([sQuery(id+"F0.wireOp",EDGE,"E25.0"),sQuery(id+"F0.wireOp",EDGE,"E25.1"),sQuery(id+"F0.wireOp",EDGE,"E25.2"),sQuery(id+"F0.wireOp",EDGE,"E25.3"),sQuery(id+"F0.wireOp",EDGE,"E25.4"),sQuery(id+"F0.wireOp",EDGE,"E25.5"),sQuery(id+"F0.wireOp",EDGE,"E25.6"),sQuery(id+"F0.wireOp",EDGE,"E25.7")])],"isStart":false})})});
            extrude(context, id + "F13", {"entities" : qUnion([Q0]), "operationType" : NewBodyOperationType.REMOVE, "endBound" : BoundingType.UP_TO_SURFACE, "endBoundEntityFace" : qUnion([Q1]), "depth" : 25 * mm});
        }
        {
            var Q0;
            Q0=makeQuery(id+"F3.boolean.opBoolean","COPY",EDGE,{"derivedFrom":makeQuery(id+"F3.opExtrude","CAP_EDGE",EDGE,{"disambiguationData":[OSD([sQuery(id+"F0.wireOp",EDGE,"E25.6")])],"isStart":false})});
            var Q1;
            Q1=makeQuery(id+"F8.boolean.opBoolean","INTERSECT",EDGE,{"derivedFrom":[makeQuery(id+"F5.opExtrude","SWEPT_FACE",FACE,{"disambiguationData":[OSD([sQuery(id+"F4.wireOp",EDGE,"E30")])]}),makeQuery(id+"F8.opExtrude","CAP_FACE",FACE,{"disambiguationData":[OSD([sQuery(id+"F7.wireOp",EDGE,"E67")])],"isStart":false})]});
            var Q2;
            Q2=makeQuery(id+"F8.boolean.opBoolean","INTERSECT",EDGE,{"disambiguationData":[OD(1.0)],"derivedFrom":[makeQuery(id+"F5.opExtrude","SWEPT_FACE",FACE,{"disambiguationData":[OSD([sQuery(id+"F4.wireOp",EDGE,"E30")])]}),makeQuery(id+"F8.opExtrude","SWEPT_FACE",FACE,{"disambiguationData":[OSD([sQuery(id+"F7.wireOp",EDGE,"E67")])]})]});
            var Q3;
            {var subQ0=sQuery(id+"F4.wireOp",EDGE,"E30");Q3=makeQuery(id+"F8.boolean.opBoolean","SPLIT",EDGE,{"disambiguationData":[TD([makeQuery(id+"F5.opExtrude","SWEPT_FACE",FACE,{"disambiguationData":[OSD([sQuery(id+"F4.wireOp",EDGE,"E35.filletArc")])]})])],"derivedFrom":makeQuery(id+"F5.opExtrude","CAP_EDGE",EDGE,{"disambiguationData":[OSD([subQ0])],"isStart":false})});}
            var Q4;
            {var subQ0=sQuery(id+"F0.wireOp",EDGE,"E25.7");var subQ1=sQuery(id+"F0.wireOp",EDGE,"E25.1");var subQ2=sQuery(id+"F0.wireOp",EDGE,"E25.6");var subQ3=sQuery(id+"F0.wireOp",EDGE,"E25.5");var subQ4=sQuery(id+"F0.wireOp",EDGE,"E25.4");var subQ5=sQuery(id+"F0.wireOp",EDGE,"E25.0");var subQ6=sQuery(id+"F0.wireOp",EDGE,"E25.2");var subQ7=sQuery(id+"F0.wireOp",EDGE,"E25.3");Q4=makeQuery(id+"F8.boolean.opBoolean","INTERSECT",EDGE,{"derivedFrom":[makeQuery(id+"F5.boolean.opBoolean","SPLIT",FACE,{"disambiguationData":[TD([makeQuery(id+"F2.opExtrude","SWEPT_FACE",FACE,{"disambiguationData":[OSD([subQ5])]})])],"derivedFrom":makeQuery(id+"F3.boolean.opBoolean","COPY",FACE,{"derivedFrom":makeQuery(id+"F3.opExtrude","CAP_FACE",FACE,{"disambiguationData":[OSD([subQ5,subQ1,subQ6,subQ7,subQ4,subQ3,subQ2,subQ0])],"isStart":false})})}),makeQuery(id+"F8.opExtrude","SWEPT_FACE",FACE,{"disambiguationData":[OSD([sQuery(id+"F7.wireOp",EDGE,"E67")])]})]});}
            var Q5;
            Q5=makeQuery(id+"F8.boolean.opBoolean","INTERSECT",EDGE,{"disambiguationData":[OD(0.0)],"derivedFrom":[makeQuery(id+"F5.opExtrude","SWEPT_FACE",FACE,{"disambiguationData":[OSD([sQuery(id+"F4.wireOp",EDGE,"E30")])]}),makeQuery(id+"F8.opExtrude","SWEPT_FACE",FACE,{"disambiguationData":[OSD([sQuery(id+"F7.wireOp",EDGE,"E67")])]})]});
            fillet(context, id + "F14", {"entities" : qUnion([Q0, Q1, Q2, Q3, Q4, Q5]), "radius" : 3 * mm, "tangentPropagation" : true, "allowEdgeOverflow" : false});
        }
        {
            var Q0;
            Q0=makeQuery(id+"F1.opExtrude","CAP_EDGE",EDGE,{"disambiguationData":[OSD([sQuery(id+"F0.wireOp",EDGE,"E1.bottom")])],"isStart":false});
            fillet(context, id + "F15", {"entities" : qUnion([Q0]), "radius" : 2 * mm, "tangentPropagation" : true, "allowEdgeOverflow" : false});
        }
        {
            var Q0;
            {var subQ0=sQuery(id+"F0.wireOp",EDGE,"E21.filletArc");var subQ1=sQuery(id+"F0.wireOp",EDGE,"E7");var subQ2=sQuery(id+"F0.wireOp",EDGE,"E6");var subQ3=sQuery(id+"F0.wireOp",EDGE,"E5");var subQ4=sQuery(id+"F0.wireOp",EDGE,"E4");var subQ5=sQuery(id+"F0.wireOp",EDGE,"E22.filletArc");var subQ6=sQuery(id+"F0.wireOp",EDGE,"E1.bottom");var subQ7=sQuery(id+"F0.wireOp",EDGE,"E1.right");var subQ8=sQuery(id+"F0.wireOp",EDGE,"E1.top");var subQ9=sQuery(id+"F0.wireOp",EDGE,"E1.left");var subQ10=sQuery(id+"F0.wireOp",EDGE,"E23.filletArc");var subQ11=sQuery(id+"F0.wireOp",EDGE,"E24.filletArc");Q0=makeQuery(id+"F2.boolean.opBoolean","SPLIT",FACE,{"disambiguationData":[TD([makeQuery(id+"F1.opExtrude","SWEPT_FACE",FACE,{"disambiguationData":[OSD([subQ6])]})])],"derivedFrom":makeQuery(id+"F1.opExtrude","CAP_FACE",FACE,{"disambiguationData":[OSD([subQ6,subQ8,subQ9,subQ7,subQ4,subQ3,subQ2,subQ1,subQ0,subQ5,subQ10,subQ11])],"isStart":true})});}
            var sketch = newSketch(context, id + "F16", { "sketchPlane" : qUnion([Q0])});
            skLineSegment(sketch, "E79.0", {"start": v(-60, 40.3) * mm, "end": v(-60, -40.3) * mm});
            skArc(sketch, "E79.1", {"start": v(-56.15, 48.18) * mm, "mid": v(-58.99, 44.68) * mm, "end": v(-60, 40.3) * mm});
            skArc(sketch, "E79.2", {"start": v(56.15, 48.18) * mm, "mid": v(0, 67.5) * mm, "end": v(-56.15, 48.18) * mm});
            skArc(sketch, "E79.3", {"start": v(60, 40.3) * mm, "mid": v(58.99, 44.68) * mm, "end": v(56.15, 48.18) * mm});
            skLineSegment(sketch, "E79.4", {"start": v(60, 40.3) * mm, "end": v(60, -40.3) * mm});
            skArc(sketch, "E79.5", {"start": v(56.15, -48.18) * mm, "mid": v(58.99, -44.68) * mm, "end": v(60, -40.3) * mm});
            skArc(sketch, "E79.6", {"start": v(-56.15, -48.18) * mm, "mid": v(0, -67.5) * mm, "end": v(56.15, -48.18) * mm});
            skArc(sketch, "E79.7", {"start": v(-60, -40.3) * mm, "mid": v(-58.99, -44.68) * mm, "end": v(-56.15, -48.18) * mm});
            skLineSegment(sketch, "E79.8", {"start": v(-80, -80) * mm, "end": v(-80, 80) * mm});
            skArc(sketch, "E79.9", {"start": v(-80, -80) * mm, "mid": v(-77.07, -87.07) * mm, "end": v(-70, -90) * mm});
            skLineSegment(sketch, "E79.10", {"start": v(-70, -90) * mm, "end": v(70, -90) * mm});
            skArc(sketch, "E79.11", {"start": v(-70, 90) * mm, "mid": v(-77.07, 87.07) * mm, "end": v(-80, 80) * mm});
            skLineSegment(sketch, "E79.12", {"start": v(-70, 90) * mm, "end": v(70, 90) * mm});
            skArc(sketch, "E79.13", {"start": v(80, 80) * mm, "mid": v(77.07, 87.07) * mm, "end": v(70, 90) * mm});
            skLineSegment(sketch, "E79.14", {"start": v(80, -80) * mm, "end": v(80, 80) * mm});
            skArc(sketch, "E79.15", {"start": v(70, -90) * mm, "mid": v(77.07, -87.07) * mm, "end": v(80, -80) * mm});
            skPoint(sketch, "E79.16", {"position": v(-58.99, -44.68) * mm});
            skCircle(sketch, "E80.0", {"center": v(60, 67.5) * mm, "radius": 4 * mm});
            skCircle(sketch, "E80.1", {"center": v(60, -67.5) * mm, "radius": 4 * mm});
            skCircle(sketch, "E80.2", {"center": v(-60, -67.5) * mm, "radius": 4 * mm});
            skCircle(sketch, "E80.3", {"center": v(-60, 67.5) * mm, "radius": 4 * mm});
            skLineSegment(sketch, "E81", {"start": v(0, 90) * mm, "end": v(0, 120) * mm, "construction": true});
            skCircle(sketch, "E82", {"center": v(0, 120) * mm, "radius": 6 * mm});
            skArc(sketch, "E83", {"start": v(15, 120) * mm, "mid": v(0, 135) * mm, "end": v(-15, 120) * mm});
            skLineSegment(sketch, "E84", {"start": v(-15, 120) * mm, "end": v(-15, 108) * mm});
            skLineSegment(sketch, "E85", {"start": v(-15, 108) * mm, "end": v(-33, 90) * mm});
            skLineSegment(sketch, "E86", {"start": v(-80, 0) * mm, "end": v(80, 0) * mm, "construction": true});
            skArc(sketch, "E87.MirrorCS", {"start": v(-15, 120) * mm, "mid": v(0, 135) * mm, "end": v(15, 120) * mm});
            skLineSegment(sketch, "E88.MirrorCS", {"start": v(15, 108) * mm, "end": v(33, 90) * mm});
            skLineSegment(sketch, "E89.MirrorCS", {"start": v(15, 120) * mm, "end": v(15, 108) * mm});
            skLineSegment(sketch, "E90.MirrorCS", {"start": v(70, 90) * mm, "end": v(-70, 90) * mm});
            skLineSegment(sketch, "E91.MirrorCS", {"start": v(70, -90) * mm, "end": v(-70, -90) * mm});
            skLineSegment(sketch, "E92.MirrorCS", {"start": v(15, -120) * mm, "end": v(15, -108) * mm});
            skLineSegment(sketch, "E93.MirrorCS", {"start": v(-15, -120) * mm, "end": v(-15, -108) * mm});
            skCircle(sketch, "E94.MirrorC", {"center": v(0, -120) * mm, "radius": 6 * mm});
            skArc(sketch, "E95.MirrorCS", {"start": v(-15, -120) * mm, "mid": v(0, -135) * mm, "end": v(15, -120) * mm});
            skArc(sketch, "E96.MirrorCS", {"start": v(15, -120) * mm, "mid": v(0, -135) * mm, "end": v(-15, -120) * mm});
            skLineSegment(sketch, "E97.MirrorCS", {"start": v(15, -108) * mm, "end": v(33, -90) * mm});
            skLineSegment(sketch, "E98.MirrorCS", {"start": v(0, -90) * mm, "end": v(0, -120) * mm, "construction": true});
            skLineSegment(sketch, "E99.MirrorCS", {"start": v(-15, -108) * mm, "end": v(-33, -90) * mm});
            skSolve(sketch);
        }
        {
            var Q0;
            Q0=makeQuery(id+"F16.imprint","IMPRINT",FACE,{"disambiguationData":[TD([[makeQuery(id+"F16.imprint","IMPRINT",EDGE,{"derivedFrom":sQuery(id+"F16.wireOp",EDGE,"E79.0")}),-1.0]])]});
            var Q1;
            {var subQ1=sQuery(id+"F16.wireOp",EDGE,"E85");Q1=makeQuery(id+"F16.imprint","IMPRINT",FACE,{"disambiguationData":[TD([[makeQuery(id+"F16.imprint","IMPRINT",EDGE,{"derivedFrom":subQ1}),1.0]])]});}
            var Q2;
            Q2=makeQuery(id+"F16.imprint","IMPRINT",FACE,{"disambiguationData":[TD([[makeQuery(id+"F16.imprint","IMPRINT",EDGE,{"derivedFrom":sQuery(id+"F16.wireOp",EDGE,"E92.MirrorCS")}),1.0]])]});
            var Q3;
            Q3=makeQuery(id+"F2.opExtrude","CAP_FACE",FACE,{"disambiguationData":[OSD([sQuery(id+"F0.wireOp",EDGE,"E12"),sQuery(id+"F0.wireOp",EDGE,"E13"),sQuery(id+"F0.wireOp",EDGE,"E14"),sQuery(id+"F0.wireOp",EDGE,"E15"),sQuery(id+"F0.wireOp",EDGE,"E17.filletArc"),sQuery(id+"F0.wireOp",EDGE,"E18.filletArc"),sQuery(id+"F0.wireOp",EDGE,"E19.filletArc"),sQuery(id+"F0.wireOp",EDGE,"E20.filletArc"),sQuery(id+"F0.wireOp",EDGE,"E25.0"),sQuery(id+"F0.wireOp",EDGE,"E25.1"),sQuery(id+"F0.wireOp",EDGE,"E25.2"),sQuery(id+"F0.wireOp",EDGE,"E25.3"),sQuery(id+"F0.wireOp",EDGE,"E25.4"),sQuery(id+"F0.wireOp",EDGE,"E25.5"),sQuery(id+"F0.wireOp",EDGE,"E25.6"),sQuery(id+"F0.wireOp",EDGE,"E25.7")])],"isStart":false});
            extrude(context, id + "F17", {"entities" : qUnion([Q0, Q1, Q2]), "endBound" : BoundingType.UP_TO_SURFACE, "endBoundEntityFace" : qUnion([Q3]), "depth" : 25 * mm});
        }
    });
